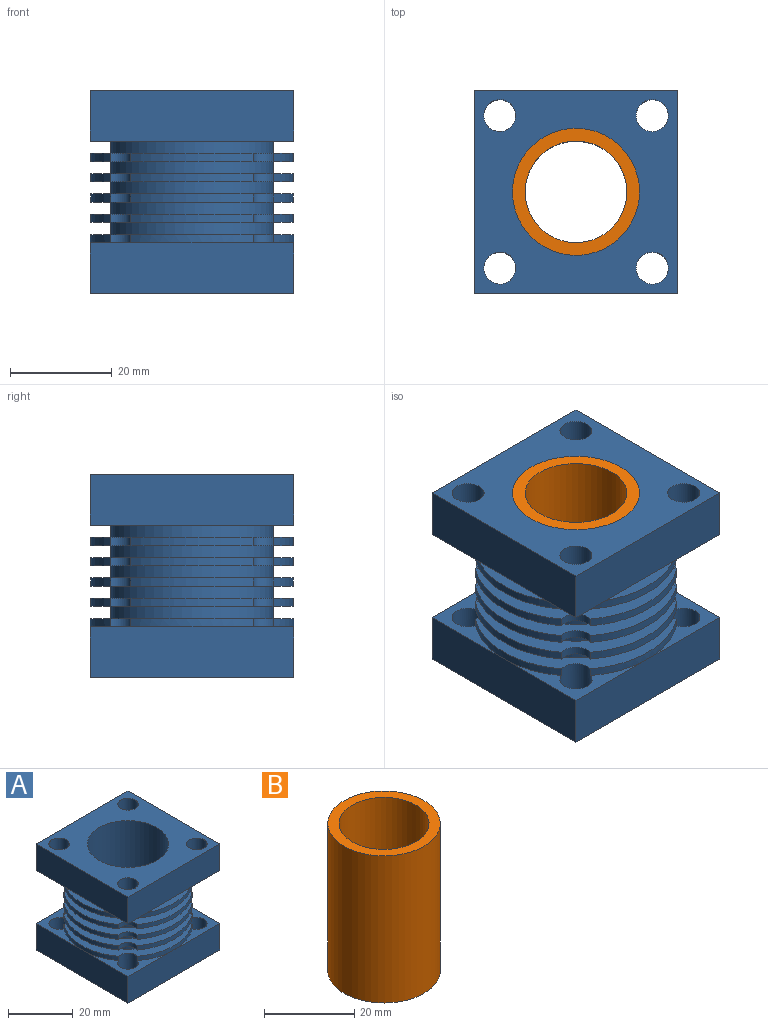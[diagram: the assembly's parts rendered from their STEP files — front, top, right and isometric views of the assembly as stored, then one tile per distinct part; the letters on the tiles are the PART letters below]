
ASSEMBLY  parts=2 mates=1
PART A: 74 faces, bbox 40x40x40 mm
  f0: cylinder r=20mm len=24.02mm, axis (0,0,-1), area 41.7mm2, adj f30,f31,f55,f73
  f1: cylinder r=20mm len=24.02mm, axis (0,0,-1), area 41.7mm2, adj f30,f31,f67,f73
  f2: cylinder r=20mm len=24.02mm, axis (0,0,-1), area 41.7mm2, adj f20,f28,f33,f54,f72
  f3: cylinder r=20mm len=24.02mm, axis (0,0,-1), area 41.7mm2, adj f22,f28,f33,f66,f72
  f4: cylinder r=20mm len=24.02mm, axis (0,0,-1), area 41.7mm2, adj f35,f36,f53,f71
  f5: cylinder r=20mm len=24.02mm, axis (0,0,-1), area 41.7mm2, adj f35,f36,f65,f71
  f6: cylinder r=20mm len=24.02mm, axis (0,0,-1), area 41.7mm2, adj f38,f39,f52,f70
  f7: cylinder r=20mm len=24.02mm, axis (0,0,-1), area 41.7mm2, adj f38,f39,f64,f70
  f8: cylinder r=20mm len=24.02mm, axis (0,0,-1), area 41.7mm2, adj f41,f42,f51,f69
  f9: cylinder r=20mm len=24.02mm, axis (0,0,-1), area 41.7mm2, adj f41,f42,f63,f69
  f10: cylinder r=20mm len=24.02mm, axis (0,0,-1), area 41.7mm2, adj f30,f31,f61,f67
  f11: cylinder r=20mm len=24.02mm, axis (0,0,-1), area 41.7mm2, adj f21,f22,f33,f60,f66
  f12: cylinder r=20mm len=24.02mm, axis (0,0,-1), area 41.7mm2, adj f35,f36,f59,f65
  f13: cylinder r=20mm len=24.02mm, axis (0,0,-1), area 41.7mm2, adj f38,f39,f58,f64
  f14: cylinder r=20mm len=24.02mm, axis (0,0,-1), area 41.7mm2, adj f41,f42,f57,f63
  f15: cylinder r=20mm len=24.02mm, axis (0,0,-1), area 41.7mm2, adj f30,f31,f55,f61
  f16: cylinder r=20mm len=24.02mm, axis (0,0,-1), area 41.7mm2, adj f20,f21,f33,f54,f60
  f17: cylinder r=20mm len=24.02mm, axis (0,0,-1), area 41.7mm2, adj f35,f36,f53,f59
  f18: cylinder r=20mm len=24.02mm, axis (0,0,-1), area 41.7mm2, adj f38,f39,f52,f58
  f19: cylinder r=20mm len=24.02mm, axis (0,0,-1), area 41.7mm2, adj f41,f42,f51,f57
  f20: plane 20x20mm, normal (0,0,1), area 62.4mm2, adj f2,f16,f24,f25,f54
  f21: plane 20x20mm, normal (0,0,1), area 62.4mm2, adj f11,f16,f23,f24,f60
  f22: plane 20x20mm, normal (0,0,1), area 62.4mm2, adj f3,f11,f23,f27,f66
  f23: plane 40x10mm, normal (1,0,0), area 400mm2, adj f21,f22,f24,f27,f29
  f24: plane 40x10mm, normal (0,1,0), area 400mm2, adj f20,f21,f23,f25,f29
  f25: plane 40x10mm, normal (-1,0,0), area 400mm2, adj f20,f24,f27,f28,f29
  f26: cylinder r=12.5mm len=40mm, axis (0,0,-1), area 3141.6mm2, adj f29,f48
  f27: plane 40x10mm, normal (0,-1,0), area 400mm2, adj f22,f23,f25,f28,f29
  f28: plane 20x20mm, normal (0,0,1), area 62.4mm2, adj f2,f3,f25,f27,f72
  f29: plane 40x40mm, normal (0,0,-1), area 984.4mm2, adj f23,f24,f25,f26,f27,f54,f60,f66
  f30: plane 40x40mm, normal (0,0,1), area 421.4mm2, adj f0,f1,f10,f15,f43,f55,f61,f67
  f31: plane 40x40mm, normal (0,0,-1), area 421.4mm2, adj f0,f1,f10,f15,f32,f55,f61,f67
  f32: cylinder r=16mm len=32mm, axis (0,0,-1), area 239.3mm2, adj f31,f33
  f33: plane 40x40mm, normal (0,0,1), area 421.4mm2, adj f2,f3,f11,f16,f32,f54,f60,f66
  f34: cylinder r=16mm len=32mm, axis (0,0,-1), area 239.3mm2, adj f35,f49
  f35: plane 40x40mm, normal (0,0,1), area 421.4mm2, adj f4,f5,f12,f17,f34,f53,f59,f65
  f36: plane 40x40mm, normal (0,0,-1), area 421.4mm2, adj f4,f5,f12,f17,f37,f53,f59,f65
  f37: cylinder r=16mm len=32mm, axis (0,0,-1), area 239.3mm2, adj f36,f38
  f38: plane 40x40mm, normal (0,0,1), area 421.4mm2, adj f6,f7,f13,f18,f37,f52,f58,f64
  f39: plane 40x40mm, normal (0,0,-1), area 421.4mm2, adj f6,f7,f13,f18,f40,f52,f58,f64
  f40: cylinder r=16mm len=32mm, axis (0,0,-1), area 239.3mm2, adj f39,f41
  f41: plane 40x40mm, normal (0,0,1), area 421.4mm2, adj f8,f9,f14,f19,f40,f51,f57,f63
  f42: plane 40x40mm, normal (0,0,-1), area 421.4mm2, adj f8,f9,f14,f19,f43,f51,f57,f63
  f43: cylinder r=16mm len=32mm, axis (0,0,-1), area 239.3mm2, adj f30,f42
  f44: plane 40x10mm, normal (1,0,0), area 400mm2, adj f45,f47,f48,f49
  f45: plane 40x10mm, normal (0,1,0), area 400mm2, adj f44,f46,f48,f49
  f46: plane 40x10mm, normal (-1,0,0), area 400mm2, adj f45,f47,f48,f49
  f47: plane 40x10mm, normal (0,-1,0), area 400mm2, adj f44,f46,f48,f49
  f48: plane 40x40mm, normal (0,0,1), area 984.4mm2, adj f26,f44,f45,f46,f47,f50,f56,f62
  f49: plane 40x40mm, normal (0,0,-1), area 671.1mm2, adj f34,f44,f45,f46,f47,f50,f56,f62
  f50: cylinder r=3.15mm len=10mm, axis (0,0,1), area 197.9mm2, adj f48,f49
  f51: cylinder r=3.15mm len=4.14mm, axis (0,0,1), area 11.3mm2, adj f8,f19,f41,f42
  f52: cylinder r=3.15mm len=4.14mm, axis (0,0,1), area 11.3mm2, adj f6,f18,f38,f39
  f53: cylinder r=3.15mm len=4.14mm, axis (0,0,1), area 11.3mm2, adj f4,f17,f35,f36
  f54: cylinder r=3.15mm len=11.62mm, axis (0,0,1), area 209.2mm2, adj f2,f16,f20,f29,f33
  f55: cylinder r=3.15mm len=4.14mm, axis (0,0,1), area 11.3mm2, adj f0,f15,f30,f31
  f56: cylinder r=3.15mm len=10mm, axis (0,0,1), area 197.9mm2, adj f48,f49
  f57: cylinder r=3.15mm len=4.14mm, axis (0,0,1), area 11.3mm2, adj f14,f19,f41,f42
  f58: cylinder r=3.15mm len=4.14mm, axis (0,0,1), area 11.3mm2, adj f13,f18,f38,f39
  f59: cylinder r=3.15mm len=4.14mm, axis (0,0,1), area 11.3mm2, adj f12,f17,f35,f36
  f60: cylinder r=3.15mm len=11.62mm, axis (0,0,1), area 209.2mm2, adj f11,f16,f21,f29,f33
  f61: cylinder r=3.15mm len=4.14mm, axis (0,0,1), area 11.3mm2, adj f10,f15,f30,f31
  f62: cylinder r=3.15mm len=10mm, axis (0,0,1), area 197.9mm2, adj f48,f49
  f63: cylinder r=3.15mm len=4.14mm, axis (0,0,1), area 11.3mm2, adj f9,f14,f41,f42
  f64: cylinder r=3.15mm len=4.14mm, axis (0,0,1), area 11.3mm2, adj f7,f13,f38,f39
  f65: cylinder r=3.15mm len=4.14mm, axis (0,0,1), area 11.3mm2, adj f5,f12,f35,f36
  f66: cylinder r=3.15mm len=11.62mm, axis (0,0,1), area 209.2mm2, adj f3,f11,f22,f29,f33
  f67: cylinder r=3.15mm len=4.14mm, axis (0,0,1), area 11.3mm2, adj f1,f10,f30,f31
  f68: cylinder r=3.15mm len=10mm, axis (0,0,1), area 197.9mm2, adj f48,f49
  f69: cylinder r=3.15mm len=4.14mm, axis (0,0,1), area 11.3mm2, adj f8,f9,f41,f42
  f70: cylinder r=3.15mm len=4.14mm, axis (0,0,1), area 11.3mm2, adj f6,f7,f38,f39
  f71: cylinder r=3.15mm len=4.14mm, axis (0,0,1), area 11.3mm2, adj f4,f5,f35,f36
  f72: cylinder r=3.15mm len=11.62mm, axis (0,0,1), area 209.2mm2, adj f2,f3,f28,f29,f33
  f73: cylinder r=3.15mm len=4.14mm, axis (0,0,1), area 11.3mm2, adj f0,f1,f30,f31
PART B: 4 faces, bbox 25x25x40 mm
  f0: cylinder r=10mm len=40mm, axis (0,0,-1), area 2513.3mm2, adj f2,f3
  f1: cylinder r=12.5mm len=40mm, axis (0,0,-1), area 3141.6mm2, adj f2,f3
  f2: plane 25x25mm, normal (0,0,1), area 176.7mm2, adj f0,f1
  f3: plane 25x25mm, normal (0,0,-1), area 176.7mm2, adj f0,f1
PLACE A at identity
PLACE B at identity
MATE fastened B.f0 <-> A.f0  axis (0,0,-1) through (0,0,40)mm
